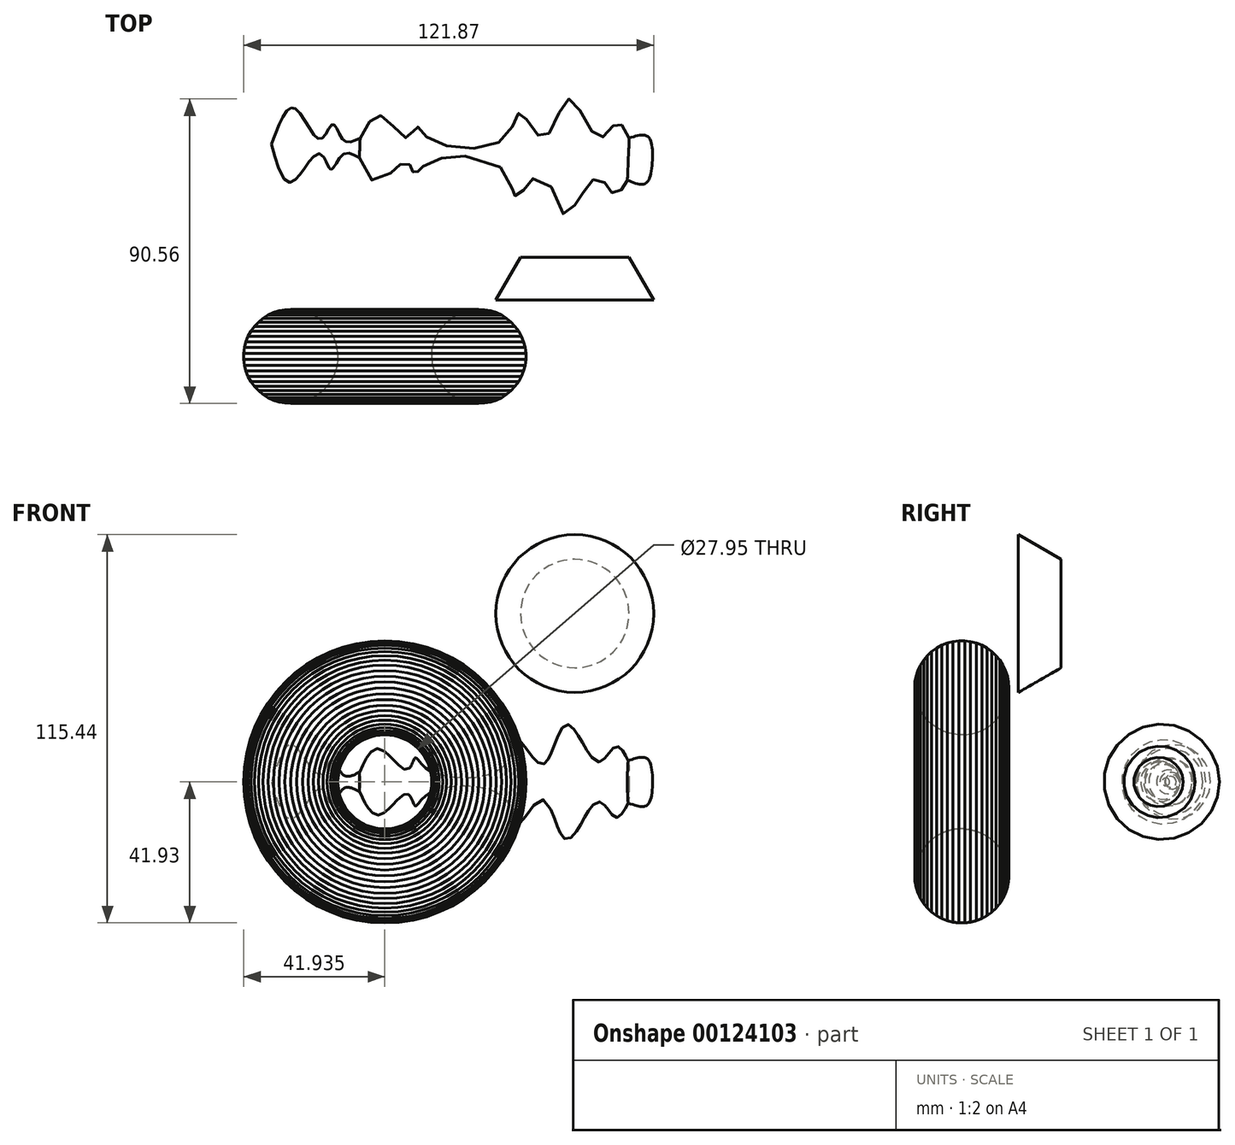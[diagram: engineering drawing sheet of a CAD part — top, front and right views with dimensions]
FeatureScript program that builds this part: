
annotation { "Feature Type Name" : "Feature", "Feature Type Description" : "" }
export const myFeature = defineFeature(function(context is Context, id is Id, definition is map)
    precondition{}
    {
        {
            var Q0;
            Q0=qCreatedBy(makeId("Top.planeOp"),FACE);
            var sketch = newSketch(context, id + "F0", { "sketchPlane" : qUnion([Q0])});
            skFitSpline(sketch, "E0", {"points": [v(-57.34, 33.54) * mm, v(-50.44, 44.2) * mm, v(-42.92, 35.11) * mm, v(-39.15, 39.5) * mm, v(-36.02, 34.8) * mm, v(-31, 35.43) * mm], "startDerivative": vector(25.58, 70.6) * mm, "endDerivative": vector(34.74, 17.08) * mm});
            skFitSpline(sketch, "E1", {"points": [v(-31, 35.43) * mm, v(-24.73, 42.01) * mm, v(-16.89, 35.43) * mm, v(-14.38, 38.88) * mm, v(-10.93, 35.43) * mm, v(11.96, 35.43) * mm, v(16.67, 42.95) * mm, v(23.57, 35.43) * mm, v(31.1, 47.03) * mm, v(39.88, 35.43) * mm, v(45.2, 39.82) * mm, v(48.97, 35.43) * mm], "startDerivative": vector(64.17, 125.52) * mm, "endDerivative": vector(49.98, -105.53) * mm});
            skFitSpline(sketch, "E2", {"points": [v(48.97, 35.43) * mm, v(54.93, 35.43) * mm, v(55.87, 28.84) * mm, v(55.87, 28.53) * mm], "startDerivative": vector(16.54, 5.11) * mm, "endDerivative": vector(0.1, -1.65) * mm});
            skLineSegment(sketch, "E3", {"start": v(-57.34, 33.54) * mm, "end": v(55.87, 28.84) * mm});
            skSolve(sketch);
        }
        {
            var Q0;
            Q0=makeQuery(id+"F0.imprint","IMPRINT",FACE,{"disambiguationData":[TD([[makeQuery(id+"F0.imprint","IMPRINT",EDGE,{"derivedFrom":sQuery(id+"F0.wireOp",EDGE,"E0")}),-1.0]])]});
            var Q1;
            Q1=sQuery(id+"F0.wireOp",EDGE,"E3");
            revolve(context, id + "F1", {"entities" : qUnion([Q0]), "axis" : qUnion([Q1]), "revolveType" : RevolveType.FULL});
        }
        {
            var Q0;
            Q0=qCreatedBy(makeId("Top.planeOp"),FACE);
            var sketch = newSketch(context, id + "F2", { "sketchPlane" : qUnion([Q0])});
            skCircle(sketch, "E4.cCircle", {"center": v(-51.63, -29.52) * mm, "radius": 13.98 * mm, "construction": true});
            skLineSegment(sketch, "E4.0", {"start": v(-37.65, -28.64) * mm, "end": v(-37.65, -30.4) * mm});
            skLineSegment(sketch, "E4.1", {"start": v(-37.65, -30.4) * mm, "end": v(-37.87, -32.15) * mm});
            skLineSegment(sketch, "E4.2", {"start": v(-37.87, -32.15) * mm, "end": v(-38.3, -33.85) * mm});
            skLineSegment(sketch, "E4.3", {"start": v(-38.3, -33.85) * mm, "end": v(-38.96, -35.49) * mm});
            skLineSegment(sketch, "E4.4", {"start": v(-38.96, -35.49) * mm, "end": v(-39.8, -37.03) * mm});
            skLineSegment(sketch, "E4.5", {"start": v(-39.8, -37.03) * mm, "end": v(-40.84, -38.45) * mm});
            skLineSegment(sketch, "E4.6", {"start": v(-40.84, -38.45) * mm, "end": v(-42.04, -39.73) * mm});
            skLineSegment(sketch, "E4.7", {"start": v(-42.04, -39.73) * mm, "end": v(-43.4, -40.85) * mm});
            skLineSegment(sketch, "E4.8", {"start": v(-43.4, -40.85) * mm, "end": v(-44.88, -41.8) * mm});
            skLineSegment(sketch, "E4.9", {"start": v(-44.88, -41.8) * mm, "end": v(-46.47, -42.54) * mm});
            skLineSegment(sketch, "E4.10", {"start": v(-46.47, -42.54) * mm, "end": v(-48.15, -43.09) * mm});
            skLineSegment(sketch, "E4.11", {"start": v(-48.15, -43.09) * mm, "end": v(-49.87, -43.42) * mm});
            skLineSegment(sketch, "E4.12", {"start": v(-49.87, -43.42) * mm, "end": v(-51.63, -43.53) * mm});
            skLineSegment(sketch, "E4.13", {"start": v(-51.63, -43.53) * mm, "end": v(-53.38, -43.42) * mm});
            skLineSegment(sketch, "E4.14", {"start": v(-53.38, -43.42) * mm, "end": v(-55.11, -43.09) * mm});
            skLineSegment(sketch, "E4.15", {"start": v(-55.11, -43.09) * mm, "end": v(-56.78, -42.54) * mm});
            skLineSegment(sketch, "E4.16", {"start": v(-56.78, -42.54) * mm, "end": v(-58.38, -41.8) * mm});
            skLineSegment(sketch, "E4.17", {"start": v(-58.38, -41.8) * mm, "end": v(-59.86, -40.85) * mm});
            skLineSegment(sketch, "E4.18", {"start": v(-59.86, -40.85) * mm, "end": v(-61.22, -39.73) * mm});
            skLineSegment(sketch, "E4.19", {"start": v(-61.22, -39.73) * mm, "end": v(-62.42, -38.45) * mm});
            skLineSegment(sketch, "E4.20", {"start": v(-62.42, -38.45) * mm, "end": v(-63.45, -37.03) * mm});
            skLineSegment(sketch, "E4.21", {"start": v(-63.45, -37.03) * mm, "end": v(-64.3, -35.49) * mm});
            skLineSegment(sketch, "E4.22", {"start": v(-64.3, -35.49) * mm, "end": v(-64.95, -33.85) * mm});
            skLineSegment(sketch, "E4.23", {"start": v(-64.95, -33.85) * mm, "end": v(-65.38, -32.15) * mm});
            skLineSegment(sketch, "E4.24", {"start": v(-65.38, -32.15) * mm, "end": v(-65.6, -30.4) * mm});
            skLineSegment(sketch, "E4.25", {"start": v(-65.6, -30.4) * mm, "end": v(-65.6, -28.64) * mm});
            skLineSegment(sketch, "E4.26", {"start": v(-65.6, -28.64) * mm, "end": v(-65.38, -26.9) * mm});
            skLineSegment(sketch, "E4.27", {"start": v(-65.38, -26.9) * mm, "end": v(-64.95, -25.2) * mm});
            skLineSegment(sketch, "E4.28", {"start": v(-64.95, -25.2) * mm, "end": v(-64.3, -23.56) * mm});
            skLineSegment(sketch, "E4.29", {"start": v(-64.3, -23.56) * mm, "end": v(-63.45, -22.02) * mm});
            skLineSegment(sketch, "E4.30", {"start": v(-63.45, -22.02) * mm, "end": v(-62.42, -20.6) * mm});
            skLineSegment(sketch, "E4.31", {"start": v(-62.42, -20.6) * mm, "end": v(-61.22, -19.31) * mm});
            skLineSegment(sketch, "E4.32", {"start": v(-61.22, -19.31) * mm, "end": v(-59.86, -18.2) * mm});
            skLineSegment(sketch, "E4.33", {"start": v(-59.86, -18.2) * mm, "end": v(-58.38, -17.25) * mm});
            skLineSegment(sketch, "E4.34", {"start": v(-58.38, -17.25) * mm, "end": v(-56.78, -16.5) * mm});
            skLineSegment(sketch, "E4.35", {"start": v(-56.78, -16.5) * mm, "end": v(-55.11, -15.96) * mm});
            skLineSegment(sketch, "E4.36", {"start": v(-55.11, -15.96) * mm, "end": v(-53.38, -15.63) * mm});
            skLineSegment(sketch, "E4.37", {"start": v(-53.38, -15.63) * mm, "end": v(-51.63, -15.52) * mm});
            skLineSegment(sketch, "E4.38", {"start": v(-51.63, -15.52) * mm, "end": v(-49.87, -15.63) * mm});
            skLineSegment(sketch, "E4.39", {"start": v(-49.87, -15.63) * mm, "end": v(-48.15, -15.96) * mm});
            skLineSegment(sketch, "E4.40", {"start": v(-48.15, -15.96) * mm, "end": v(-46.47, -16.5) * mm});
            skLineSegment(sketch, "E4.41", {"start": v(-46.47, -16.5) * mm, "end": v(-44.88, -17.25) * mm});
            skLineSegment(sketch, "E4.42", {"start": v(-44.88, -17.25) * mm, "end": v(-43.4, -18.2) * mm});
            skLineSegment(sketch, "E4.43", {"start": v(-43.4, -18.2) * mm, "end": v(-42.04, -19.31) * mm});
            skLineSegment(sketch, "E4.44", {"start": v(-42.04, -19.31) * mm, "end": v(-40.84, -20.6) * mm});
            skLineSegment(sketch, "E4.45", {"start": v(-40.84, -20.6) * mm, "end": v(-39.8, -22.02) * mm});
            skLineSegment(sketch, "E4.46", {"start": v(-39.8, -22.02) * mm, "end": v(-38.96, -23.56) * mm});
            skLineSegment(sketch, "E4.47", {"start": v(-38.96, -23.56) * mm, "end": v(-38.3, -25.2) * mm});
            skLineSegment(sketch, "E4.48", {"start": v(-38.3, -25.2) * mm, "end": v(-37.87, -26.9) * mm});
            skLineSegment(sketch, "E4.49", {"start": v(-37.87, -26.9) * mm, "end": v(-37.65, -28.64) * mm});
            skPoint(sketch, "E4.0.midPoint", {"position": v(-37.65, -29.52) * mm});
            skLineSegment(sketch, "E5", {"start": v(-23.67, -46.35) * mm, "end": v(-23.67, -13.83) * mm});
            skSolve(sketch);
        }
        {
            var Q0;
            Q0 = qSketchRegion(id + "F2", true);
            var Q1;
            Q1=sQuery(id+"F2.wireOp",EDGE,"E5");
            revolve(context, id + "F3", {"entities" : qUnion([Q0]), "axis" : qUnion([Q1]), "revolveType" : RevolveType.FULL});
        }
        {
            var Q0;
            Q0=qCreatedBy(makeId("Front.planeOp"),FACE);
            var sketch = newSketch(context, id + "F4", { "sketchPlane" : qUnion([Q0])});
            skCircle(sketch, "E6", {"center": v(32.8, 50.06) * mm, "radius": 16.12 * mm});
            skSolve(sketch);
        }
        {
            var Q0;
            Q0 = qSketchRegion(id + "F4", true);
            extrude(context, id + "F5", {"entities" : qUnion([Q0]), "depth" : 12.7 * mm, "hasDraft" : true, "draftAngle" : 30 * degree});
        }
    });
